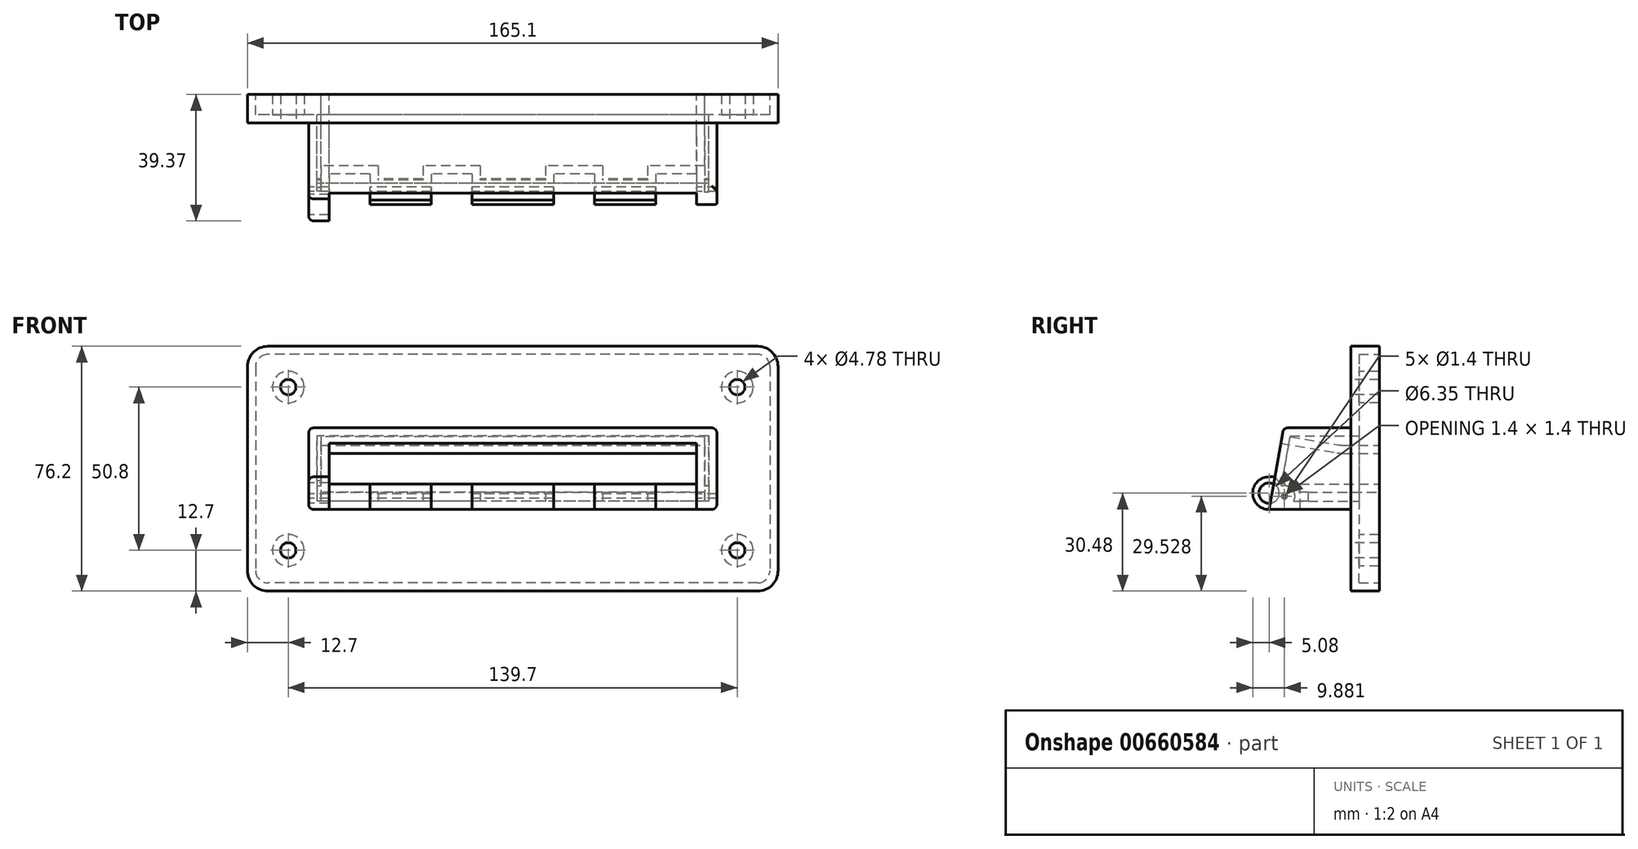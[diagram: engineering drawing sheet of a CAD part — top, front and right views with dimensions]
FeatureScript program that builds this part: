
annotation { "Feature Type Name" : "Feature", "Feature Type Description" : "" }
export const myFeature = defineFeature(function(context is Context, id is Id, definition is map)
    precondition{}
    {
        {
            var Q0;
            Q0=qCreatedBy(makeId("Front.planeOp"),FACE);
            var sketch = newSketch(context, id + "F0", { "sketchPlane" : qUnion([Q0])});
            skLineSegment(sketch, "E0.bottom", {"start": v(82.55, 38.1) * mm, "end": v(-82.55, 38.1) * mm});
            skLineSegment(sketch, "E0.top", {"start": v(82.55, -38.1) * mm, "end": v(-82.55, -38.1) * mm});
            skLineSegment(sketch, "E0.left", {"start": v(82.55, 38.1) * mm, "end": v(82.55, -38.1) * mm});
            skLineSegment(sketch, "E0.right", {"start": v(-82.55, 38.1) * mm, "end": v(-82.55, -38.1) * mm});
            skPoint(sketch, "E0.middle", {"position": v(0, 0) * mm});
            skSolve(sketch);
        }
        {
            var Q0;
            Q0=makeQuery(id+"F0.imprint","IMPRINT",FACE,{"disambiguationData":[TD([[makeQuery(id+"F0.imprint","IMPRINT",EDGE,{"derivedFrom":sQuery(id+"F0.wireOp",EDGE,"E0.bottom")}),1.0]])]});
            extrude(context, id + "F1", {"entities" : qUnion([Q0]), "depth" : 34.3 * mm, "offsetDistance" : 25.4 * mm});
        }
        {
            var Q0;
            Q0=makeQuery(id+"F1.opExtrude","CAP_FACE",FACE,{"disambiguationData":[OSD([sQuery(id+"F0.wireOp",EDGE,"E0.bottom"),sQuery(id+"F0.wireOp",EDGE,"E0.top"),sQuery(id+"F0.wireOp",EDGE,"E0.left"),sQuery(id+"F0.wireOp",EDGE,"E0.right")])],"isStart":false});
            var sketch = newSketch(context, id + "F2", { "sketchPlane" : qUnion([Q0])});
            skLineSegment(sketch, "E1.bottom", {"start": v(63.5, 12.7) * mm, "end": v(-63.5, 12.7) * mm});
            skLineSegment(sketch, "E1.top", {"start": v(63.5, -12.7) * mm, "end": v(-63.5, -12.7) * mm});
            skLineSegment(sketch, "E1.left", {"start": v(63.5, 12.7) * mm, "end": v(63.5, -12.7) * mm});
            skLineSegment(sketch, "E1.right", {"start": v(-63.5, 12.7) * mm, "end": v(-63.5, -12.7) * mm});
            skPoint(sketch, "E1.middle", {"position": v(0, 0) * mm});
            skLineSegment(sketch, "E2.bottom", {"start": v(82.55, 38.1) * mm, "end": v(-82.55, 38.1) * mm});
            skLineSegment(sketch, "E2.top", {"start": v(82.55, -38.1) * mm, "end": v(-82.55, -38.1) * mm});
            skLineSegment(sketch, "E2.left", {"start": v(82.55, 38.1) * mm, "end": v(82.55, -38.1) * mm});
            skLineSegment(sketch, "E2.right", {"start": v(-82.55, 38.1) * mm, "end": v(-82.55, -38.1) * mm});
            skSolve(sketch);
        }
        {
            var Q0;
            Q0=makeQuery(id+"F2.imprint","IMPRINT",FACE,{"disambiguationData":[TD([[makeQuery(id+"F2.imprint","IMPRINT",EDGE,{"derivedFrom":sQuery(id+"F2.wireOp",EDGE,"E1.bottom")}),-1.0]])]});
            extrude(context, id + "F3", {"entities" : qUnion([Q0]), "operationType" : NewBodyOperationType.REMOVE, "oppositeDirection" : true, "depth" : 25.4 * mm, "offsetDistance" : 25.4 * mm});
        }
        {
            var Q0;
            Q0=makeQuery(id+"F1.opExtrude","CAP_FACE",FACE,{"disambiguationData":[OSD([sQuery(id+"F0.wireOp",EDGE,"E0.bottom"),sQuery(id+"F0.wireOp",EDGE,"E0.top"),sQuery(id+"F0.wireOp",EDGE,"E0.left"),sQuery(id+"F0.wireOp",EDGE,"E0.right")])],"isStart":true});
            var sketch = newSketch(context, id + "F4", { "sketchPlane" : qUnion([Q0])});
            skLineSegment(sketch, "E3.bottom", {"start": v(57.15, 4.76) * mm, "end": v(-57.15, 4.76) * mm});
            skLineSegment(sketch, "E3.top", {"start": v(57.15, -4.76) * mm, "end": v(-57.15, -4.76) * mm});
            skLineSegment(sketch, "E3.left", {"start": v(57.15, 4.76) * mm, "end": v(57.15, -4.76) * mm});
            skLineSegment(sketch, "E3.right", {"start": v(-57.15, 4.76) * mm, "end": v(-57.15, -4.76) * mm});
            skPoint(sketch, "E3.middle", {"position": v(0, 0) * mm});
            skSolve(sketch);
        }
        {
            var Q0;
            Q0=makeQuery(id+"F4.imprint","IMPRINT",FACE,{"disambiguationData":[TD([[makeQuery(id+"F4.imprint","IMPRINT",EDGE,{"derivedFrom":sQuery(id+"F4.wireOp",EDGE,"E3.bottom")}),1.0]])]});
            extrude(context, id + "F5", {"entities" : qUnion([Q0]), "operationType" : NewBodyOperationType.REMOVE, "endBound" : BoundingType.THROUGH_ALL, "oppositeDirection" : true, "depth" : 25.4 * mm, "offsetDistance" : 25.4 * mm});
        }
        {
            var Q0;
            Q0=makeQuery(id+"F1.opExtrude","CAP_FACE",FACE,{"disambiguationData":[OSD([sQuery(id+"F0.wireOp",EDGE,"E0.bottom"),sQuery(id+"F0.wireOp",EDGE,"E0.top"),sQuery(id+"F0.wireOp",EDGE,"E0.left"),sQuery(id+"F0.wireOp",EDGE,"E0.right")])],"isStart":false});
            var sketch = newSketch(context, id + "F6", { "sketchPlane" : qUnion([Q0])});
            skLineSegment(sketch, "E4.bottom", {"start": v(-57.15, -4.76) * mm, "end": v(-44.45, -4.76) * mm});
            skLineSegment(sketch, "E4.top", {"start": v(-57.15, -12.7) * mm, "end": v(-44.45, -12.7) * mm});
            skLineSegment(sketch, "E4.left", {"start": v(-57.15, -4.76) * mm, "end": v(-57.15, -12.7) * mm});
            skLineSegment(sketch, "E4.right", {"start": v(-44.45, -4.76) * mm, "end": v(-44.45, -12.7) * mm});
            skLineSegment(sketch, "E5.bottom", {"start": v(57.15, -4.76) * mm, "end": v(44.45, -4.76) * mm});
            skLineSegment(sketch, "E5.top", {"start": v(57.15, -12.7) * mm, "end": v(44.45, -12.7) * mm});
            skLineSegment(sketch, "E5.left", {"start": v(57.15, -4.76) * mm, "end": v(57.15, -12.7) * mm});
            skLineSegment(sketch, "E5.right", {"start": v(44.45, -4.76) * mm, "end": v(44.45, -12.7) * mm});
            skLineSegment(sketch, "E6.bottom", {"start": v(-25.4, -4.76) * mm, "end": v(-12.7, -4.76) * mm});
            skLineSegment(sketch, "E6.top", {"start": v(-25.4, -12.7) * mm, "end": v(-12.7, -12.7) * mm});
            skLineSegment(sketch, "E6.left", {"start": v(-25.4, -4.76) * mm, "end": v(-25.4, -12.7) * mm});
            skLineSegment(sketch, "E6.right", {"start": v(-12.7, -4.76) * mm, "end": v(-12.7, -12.7) * mm});
            skLineSegment(sketch, "E7.bottom", {"start": v(12.7, -4.76) * mm, "end": v(25.4, -4.76) * mm});
            skLineSegment(sketch, "E7.top", {"start": v(12.7, -12.7) * mm, "end": v(25.4, -12.7) * mm});
            skLineSegment(sketch, "E7.left", {"start": v(12.7, -4.76) * mm, "end": v(12.7, -12.7) * mm});
            skLineSegment(sketch, "E7.right", {"start": v(25.4, -4.76) * mm, "end": v(25.4, -12.7) * mm});
            skSolve(sketch);
        }
        {
            var Q0;
            Q0=makeQuery(id+"F6.imprint","IMPRINT",FACE,{"disambiguationData":[TD([[makeQuery(id+"F6.imprint","IMPRINT",EDGE,{"derivedFrom":sQuery(id+"F6.wireOp",EDGE,"E4.bottom")}),1.0]])]});
            var Q1;
            Q1=makeQuery(id+"F6.imprint","IMPRINT",FACE,{"disambiguationData":[TD([[makeQuery(id+"F6.imprint","IMPRINT",EDGE,{"derivedFrom":sQuery(id+"F6.wireOp",EDGE,"E6.bottom")}),1.0]])]});
            var Q2;
            Q2=makeQuery(id+"F6.imprint","IMPRINT",FACE,{"disambiguationData":[TD([[makeQuery(id+"F6.imprint","IMPRINT",EDGE,{"derivedFrom":sQuery(id+"F6.wireOp",EDGE,"E7.bottom")}),1.0]])]});
            var Q3;
            Q3=makeQuery(id+"F6.imprint","IMPRINT",FACE,{"disambiguationData":[TD([[makeQuery(id+"F6.imprint","IMPRINT",EDGE,{"derivedFrom":sQuery(id+"F6.wireOp",EDGE,"E5.bottom")}),1.0]])]});
            extrude(context, id + "F7", {"entities" : qUnion([Q0, Q1, Q2, Q3]), "operationType" : NewBodyOperationType.REMOVE, "oppositeDirection" : true, "depth" : 9.52 * mm, "offsetDistance" : 25.4 * mm});
        }
        {
            var Q0;
            Q0=makeQuery(id+"F3.boolean.opBoolean","COPY",FACE,{"derivedFrom":makeQuery(id+"F3.opExtrude","SWEPT_FACE",FACE,{"disambiguationData":[OSD([sQuery(id+"F2.wireOp",EDGE,"E1.left")])]})});
            var sketch = newSketch(context, id + "F8", { "sketchPlane" : qUnion([Q0])});
            skLineSegment(sketch, "E8", {"start": v(-34.3, -12.7) * mm, "end": v(-29.81, 12.7) * mm});
            skLineSegment(sketch, "E9", {"start": v(-29.81, 12.7) * mm, "end": v(-34.3, 12.7) * mm});
            skLineSegment(sketch, "E10", {"start": v(-34.3, 12.7) * mm, "end": v(-34.3, -12.7) * mm});
            skSolve(sketch);
        }
        {
            var Q0;
            Q0=makeQuery(id+"F8.imprint","IMPRINT",FACE,{"disambiguationData":[TD([[makeQuery(id+"F8.imprint","IMPRINT",EDGE,{"derivedFrom":sQuery(id+"F8.wireOp",EDGE,"E8")}),1.0]])]});
            extrude(context, id + "F9", {"entities" : qUnion([Q0]), "operationType" : NewBodyOperationType.REMOVE, "endBound" : BoundingType.THROUGH_ALL, "oppositeDirection" : true, "depth" : 25.4 * mm, "offsetDistance" : 25.4 * mm});
        }
        {
            var Q0;
            Q0=makeQuery(id+"F3.boolean.opBoolean","COPY",FACE,{"derivedFrom":makeQuery(id+"F3.opExtrude","SWEPT_FACE",FACE,{"disambiguationData":[OSD([sQuery(id+"F2.wireOp",EDGE,"E1.right")])]})});
            var sketch = newSketch(context, id + "F10", { "sketchPlane" : qUnion([Q0])});
            skArc(sketch, "E11", {"start": v(34.3, -12.7) * mm, "mid": v(39.37, -7.62) * mm, "end": v(34.3, -2.54) * mm});
            skLineSegment(sketch, "E12", {"start": v(34.3, -2.54) * mm, "end": v(32.5, -2.54) * mm});
            skLineSegment(sketch, "E13", {"start": v(32.5, -2.54) * mm, "end": v(34.3, -12.7) * mm});
            skSolve(sketch);
        }
        {
            var Q0;
            Q0=makeQuery(id+"F10.imprint","IMPRINT",FACE,{"disambiguationData":[TD([[makeQuery(id+"F10.imprint","IMPRINT",EDGE,{"derivedFrom":sQuery(id+"F10.wireOp",EDGE,"E11")}),1.0]])]});
            extrude(context, id + "F11", {"entities" : qUnion([Q0]), "operationType" : NewBodyOperationType.ADD, "oppositeDirection" : true, "depth" : 6.35 * mm, "offsetDistance" : 25.4 * mm});
        }
        {
            var Q0;
            Q0=makeQuery(id+"F11.boolean.opBoolean","MERGE",FACE,{"derivedFrom":[makeQuery(id+"F3.boolean.opBoolean","COPY",FACE,{"derivedFrom":makeQuery(id+"F3.opExtrude","SWEPT_FACE",FACE,{"disambiguationData":[OSD([sQuery(id+"F2.wireOp",EDGE,"E1.right")])]})}),makeQuery(id+"F11.opExtrude","CAP_FACE",FACE,{"disambiguationData":[OSD([sQuery(id+"F10.wireOp",EDGE,"E11"),sQuery(id+"F10.wireOp",EDGE,"t9ToSJXX-xxId-XsRl-dtjL-8FJcNpwY83Oj"),sQuery(id+"F10.wireOp",EDGE,"S0cJsciV-L8RJ-brYd-5tid-K804BzsuG4tW")])],"isStart":true})]});
            var sketch = newSketch(context, id + "F12", { "sketchPlane" : qUnion([Q0])});
            skPoint(sketch, "E14", {"position": v(34.3, -7.62) * mm});
            skPoint(sketch, "E15", {"position": v(40.8, -7.72) * mm});
            skSolve(sketch);
        }
        {
            var Q0;
            Q0=sQuery(id+"F12.wireOp",VERTEX,"E14");
            var Q1;
            Q1=makeQuery(id+"F1.opExtrude","SWEPT_BODY",BODY,{"disambiguationData":[OSD([sQuery(id+"F0.wireOp",EDGE,"E0.bottom"),sQuery(id+"F0.wireOp",EDGE,"E0.top"),sQuery(id+"F0.wireOp",EDGE,"E0.left"),sQuery(id+"F0.wireOp",EDGE,"E0.right")])]});
            hole(context, id + "F13", {"style" : HoleStyle.SIMPLE, "endStyle" : HoleEndStyle.BLIND, "holeDiameter" : 6.35 * mm, "majorDiameter" : 6.35 * mm, "holeDepth" : 13.97 * mm, "isTappedThrough" : true, "tappedDepth" : 12.7 * mm, "tapClearance" : 3, "startFromSketch" : true, "locations" : qUnion([Q0]), "scope" : qUnion([Q1])});
        }
        {
            var Q0;
            Q0=makeQuery(id+"F1.opExtrude","SWEPT_EDGE",EDGE,{"disambiguationData":[OSD([sQuery(id+"F0.wireOp",EDGE,"E0.bottom"),sQuery(id+"F0.wireOp",EDGE,"E0.right")])]});
            var Q1;
            Q1=makeQuery(id+"F1.opExtrude","SWEPT_EDGE",EDGE,{"disambiguationData":[OSD([sQuery(id+"F0.wireOp",EDGE,"E0.bottom"),sQuery(id+"F0.wireOp",EDGE,"E0.left")])]});
            var Q2;
            Q2=makeQuery(id+"F1.opExtrude","SWEPT_EDGE",EDGE,{"disambiguationData":[OSD([sQuery(id+"F0.wireOp",EDGE,"E0.top"),sQuery(id+"F0.wireOp",EDGE,"E0.left")])]});
            var Q3;
            Q3=makeQuery(id+"F1.opExtrude","SWEPT_EDGE",EDGE,{"disambiguationData":[OSD([sQuery(id+"F0.wireOp",EDGE,"E0.top"),sQuery(id+"F0.wireOp",EDGE,"E0.right")])]});
            fillet(context, id + "F14", {"entities" : qUnion([Q0, Q1, Q2, Q3]), "radius" : 6.35 * mm, "tangentPropagation" : true, "allowEdgeOverflow" : false});
        }
        {
            var Q0;
            Q0=makeQuery(id+"F9.boolean.opBoolean","INTERSECT",EDGE,{"derivedFrom":[makeQuery(id+"F5.boolean.opBoolean","COPY",FACE,{"derivedFrom":makeQuery(id+"F5.opExtrude","SWEPT_FACE",FACE,{"disambiguationData":[OSD([sQuery(id+"F4.wireOp",EDGE,"E3.bottom")])]})}),makeQuery(id+"F9.opExtrude","SWEPT_FACE",FACE,{"disambiguationData":[OSD([sQuery(id+"F8.wireOp",EDGE,"E8")])]})]});
            chamfer(context, id + "F15", {"entities" : qUnion([Q0]), "chamferType" : ChamferType.TWO_OFFSETS, "width1" : 19.05 * mm, "oppositeDirection" : false, "width2" : 3.17 * mm, "tangentPropagation" : true});
        }
        {
            var Q0;
            Q0=makeQuery(id+"F3.boolean.opBoolean","COPY",FACE,{"derivedFrom":makeQuery(id+"F3.opExtrude","CAP_FACE",FACE,{"disambiguationData":[OSD([sQuery(id+"F2.wireOp",EDGE,"E1.bottom"),sQuery(id+"F2.wireOp",EDGE,"E1.top"),sQuery(id+"F2.wireOp",EDGE,"E1.left"),sQuery(id+"F2.wireOp",EDGE,"E1.right"),sQuery(id+"F2.wireOp",EDGE,"E2.bottom"),sQuery(id+"F2.wireOp",EDGE,"E2.top"),sQuery(id+"F2.wireOp",EDGE,"E2.left"),sQuery(id+"F2.wireOp",EDGE,"E2.right")])],"isStart":false})});
            var sketch = newSketch(context, id + "F16", { "sketchPlane" : qUnion([Q0])});
            skPoint(sketch, "E16", {"position": v(-69.85, 25.4) * mm});
            skPoint(sketch, "E17", {"position": v(69.85, 25.4) * mm});
            skPoint(sketch, "E18", {"position": v(69.85, -25.4) * mm});
            skPoint(sketch, "E19", {"position": v(-69.85, -25.4) * mm});
            skSolve(sketch);
        }
        {
            var Q0;
            Q0=sQuery(id+"F16.wireOp",VERTEX,"E16");
            var Q1;
            Q1=sQuery(id+"F16.wireOp",VERTEX,"E17");
            var Q2;
            Q2=sQuery(id+"F16.wireOp",VERTEX,"E18");
            var Q3;
            Q3=sQuery(id+"F16.wireOp",VERTEX,"E19");
            var Q4;
            Q4=makeQuery(id+"F1.opExtrude","SWEPT_BODY",BODY,{"disambiguationData":[OSD([sQuery(id+"F0.wireOp",EDGE,"E0.bottom"),sQuery(id+"F0.wireOp",EDGE,"E0.top"),sQuery(id+"F0.wireOp",EDGE,"E0.left"),sQuery(id+"F0.wireOp",EDGE,"E0.right")])]});
            hole(context, id + "F17", {"style" : HoleStyle.SIMPLE, "endStyle" : HoleEndStyle.THROUGH, "holeDiameter" : 4.78 * mm, "majorDiameter" : 6.35 * mm, "isTappedThrough" : true, "tappedDepth" : 12.7 * mm, "tapClearance" : 3, "startFromSketch" : true, "locations" : qUnion([Q0, Q1, Q2, Q3]), "scope" : qUnion([Q4])});
        }
        {
            var Q0;
            Q0=makeQuery(id+"F11.boolean.opBoolean","MERGE",FACE,{"derivedFrom":[makeQuery(id+"F3.boolean.opBoolean","COPY",FACE,{"derivedFrom":makeQuery(id+"F3.opExtrude","SWEPT_FACE",FACE,{"disambiguationData":[OSD([sQuery(id+"F2.wireOp",EDGE,"E1.right")])]})}),makeQuery(id+"F11.opExtrude","CAP_FACE",FACE,{"disambiguationData":[OSD([sQuery(id+"F10.wireOp",EDGE,"E11"),sQuery(id+"F10.wireOp",EDGE,"t9ToSJXX-xxId-XsRl-dtjL-8FJcNpwY83Oj"),sQuery(id+"F10.wireOp",EDGE,"S0cJsciV-L8RJ-brYd-5tid-K804BzsuG4tW")])],"isStart":true})]});
            var sketch = newSketch(context, id + "F18", { "sketchPlane" : qUnion([Q0])});
            skPoint(sketch, "E20", {"position": v(29.49, -8.57) * mm});
            skSolve(sketch);
        }
        {
            var Q0;
            Q0=sQuery(id+"F18.wireOp",VERTEX,"E20");
            var Q1;
            Q1=makeQuery(id+"F1.opExtrude","SWEPT_BODY",BODY,{"disambiguationData":[OSD([sQuery(id+"F0.wireOp",EDGE,"E0.bottom"),sQuery(id+"F0.wireOp",EDGE,"E0.top"),sQuery(id+"F0.wireOp",EDGE,"E0.left"),sQuery(id+"F0.wireOp",EDGE,"E0.right")])]});
            hole(context, id + "F19", {"style" : HoleStyle.SIMPLE, "endStyle" : HoleEndStyle.THROUGH, "holeDiameter" : 1.4 * mm, "majorDiameter" : 6.35 * mm, "isTappedThrough" : true, "tappedDepth" : 12.7 * mm, "tapClearance" : 3, "startFromSketch" : true, "locations" : qUnion([Q0]), "scope" : qUnion([Q1])});
        }
        {
            var Q0;
            Q0=makeQuery(id+"F9.boolean.opBoolean","INTERSECT",EDGE,{"derivedFrom":[makeQuery(id+"F3.boolean.opBoolean","COPY",FACE,{"derivedFrom":makeQuery(id+"F3.opExtrude","SWEPT_FACE",FACE,{"disambiguationData":[OSD([sQuery(id+"F2.wireOp",EDGE,"E1.right")])]})}),makeQuery(id+"F9.opExtrude","SWEPT_FACE",FACE,{"disambiguationData":[OSD([sQuery(id+"F8.wireOp",EDGE,"E8")])]})]});
            fillet(context, id + "F20", {"entities" : qUnion([Q0]), "radius" : 1.59 * mm, "tangentPropagation" : true, "allowEdgeOverflow" : false});
        }
        {
            var Q0;
            Q0=makeQuery(id+"F3.boolean.opBoolean","COPY",EDGE,{"derivedFrom":makeQuery(id+"F3.opExtrude","SWEPT_EDGE",EDGE,{"disambiguationData":[OSD([sQuery(id+"F2.wireOp",EDGE,"E1.bottom"),sQuery(id+"F2.wireOp",EDGE,"E1.right")])]})});
            var Q1;
            Q1=makeQuery(id+"F3.boolean.opBoolean","COPY",EDGE,{"derivedFrom":makeQuery(id+"F3.opExtrude","SWEPT_EDGE",EDGE,{"disambiguationData":[OSD([sQuery(id+"F2.wireOp",EDGE,"E1.bottom"),sQuery(id+"F2.wireOp",EDGE,"E1.left")])]})});
            var Q2;
            Q2=makeQuery(id+"F3.boolean.opBoolean","COPY",EDGE,{"derivedFrom":makeQuery(id+"F3.opExtrude","SWEPT_EDGE",EDGE,{"disambiguationData":[OSD([sQuery(id+"F2.wireOp",EDGE,"E1.top"),sQuery(id+"F2.wireOp",EDGE,"E1.left")])]})});
            var Q3;
            Q3=makeQuery(id+"F3.boolean.opBoolean","COPY",EDGE,{"derivedFrom":makeQuery(id+"F3.opExtrude","SWEPT_EDGE",EDGE,{"disambiguationData":[OSD([sQuery(id+"F2.wireOp",EDGE,"E1.top"),sQuery(id+"F2.wireOp",EDGE,"E1.right")])]})});
            fillet(context, id + "F21", {"entities" : qUnion([Q0, Q1, Q2, Q3]), "radius" : 1.59 * mm, "tangentPropagation" : true, "allowEdgeOverflow" : false});
        }
        {
            var Q0;
            {var subQ0=sQuery(id+"F8.wireOp",EDGE,"E8");Q0=makeQuery(id+"F2j6ox91vYMW6DV_1.opChamfer","BLEND_EDGE",EDGE,{"blendedFrom":[makeQuery(id+"F9.boolean.opBoolean","INTERSECT",EDGE,{"derivedFrom":[makeQuery(id+"F5.boolean.opBoolean","COPY",FACE,{"derivedFrom":makeQuery(id+"F5.opExtrude","SWEPT_FACE",FACE,{"disambiguationData":[OSD([sQuery(id+"F4.wireOp",EDGE,"E3.left")])]})}),makeQuery(id+"F9.opExtrude","SWEPT_FACE",FACE,{"disambiguationData":[OSD([subQ0])]})]}),makeQuery(id+"F15.opChamfer","BLEND_FACE",FACE,{"disambiguationData":[OSD([sQuery(id+"F4.wireOp",EDGE,"E3.bottom"),subQ0])]})],"blendedInto":[makeQuery(id+"F15.opChamfer","BLEND_FACE",FACE,{"disambiguationData":[OSD([sQuery(id+"F4.wireOp",EDGE,"E3.bottom"),subQ0])]})]});}
            var Q1;
            {var subQ0=sQuery(id+"F8.wireOp",EDGE,"E8");Q1=makeQuery(id+"F2j6ox91vYMW6DV_1.opChamfer","BLEND_EDGE",EDGE,{"blendedFrom":[makeQuery(id+"F9.boolean.opBoolean","INTERSECT",EDGE,{"derivedFrom":[makeQuery(id+"F5.boolean.opBoolean","COPY",FACE,{"derivedFrom":makeQuery(id+"F5.opExtrude","SWEPT_FACE",FACE,{"disambiguationData":[OSD([sQuery(id+"F4.wireOp",EDGE,"E3.left")])]})}),makeQuery(id+"F9.opExtrude","SWEPT_FACE",FACE,{"disambiguationData":[OSD([subQ0])]})]}),makeQuery(id+"FDbppE0EpAkwhRO_1.opChamfer","BLEND_FACE",FACE,{"disambiguationData":[OSD([sQuery(id+"F4.wireOp",EDGE,"E3.top"),subQ0])]})],"blendedInto":[makeQuery(id+"FDbppE0EpAkwhRO_1.opChamfer","BLEND_FACE",FACE,{"disambiguationData":[OSD([sQuery(id+"F4.wireOp",EDGE,"E3.top"),subQ0])]})]});}
            var Q2;
            {var subQ0=sQuery(id+"F8.wireOp",EDGE,"E8");Q2=makeQuery(id+"F2j6ox91vYMW6DV_1.opChamfer","BLEND_EDGE",EDGE,{"blendedFrom":[makeQuery(id+"F9.boolean.opBoolean","INTERSECT",EDGE,{"derivedFrom":[makeQuery(id+"F5.boolean.opBoolean","COPY",FACE,{"derivedFrom":makeQuery(id+"F5.opExtrude","SWEPT_FACE",FACE,{"disambiguationData":[OSD([sQuery(id+"F4.wireOp",EDGE,"E3.right")])]})}),makeQuery(id+"F9.opExtrude","SWEPT_FACE",FACE,{"disambiguationData":[OSD([subQ0])]})]}),makeQuery(id+"FDbppE0EpAkwhRO_1.opChamfer","BLEND_FACE",FACE,{"disambiguationData":[OSD([sQuery(id+"F4.wireOp",EDGE,"E3.top"),subQ0])]})],"blendedInto":[makeQuery(id+"FDbppE0EpAkwhRO_1.opChamfer","BLEND_FACE",FACE,{"disambiguationData":[OSD([sQuery(id+"F4.wireOp",EDGE,"E3.top"),subQ0])]})]});}
            var Q3;
            {var subQ0=sQuery(id+"F8.wireOp",EDGE,"E8");Q3=makeQuery(id+"F2j6ox91vYMW6DV_1.opChamfer","BLEND_EDGE",EDGE,{"blendedFrom":[makeQuery(id+"F9.boolean.opBoolean","INTERSECT",EDGE,{"derivedFrom":[makeQuery(id+"F5.boolean.opBoolean","COPY",FACE,{"derivedFrom":makeQuery(id+"F5.opExtrude","SWEPT_FACE",FACE,{"disambiguationData":[OSD([sQuery(id+"F4.wireOp",EDGE,"E3.right")])]})}),makeQuery(id+"F9.opExtrude","SWEPT_FACE",FACE,{"disambiguationData":[OSD([subQ0])]})]}),makeQuery(id+"F15.opChamfer","BLEND_FACE",FACE,{"disambiguationData":[OSD([sQuery(id+"F4.wireOp",EDGE,"E3.bottom"),subQ0])]})],"blendedInto":[makeQuery(id+"F15.opChamfer","BLEND_FACE",FACE,{"disambiguationData":[OSD([sQuery(id+"F4.wireOp",EDGE,"E3.bottom"),subQ0])]})]});}
            var Q4;
            {var subQ0=makeQuery(id+"F5.boolean.opBoolean","COPY",FACE,{"derivedFrom":makeQuery(id+"F5.opExtrude","SWEPT_FACE",FACE,{"disambiguationData":[OSD([sQuery(id+"F4.wireOp",EDGE,"E3.left")])]})});Q4=makeQuery(id+"F2j6ox91vYMW6DV_1.opChamfer","BLEND_EDGE",EDGE,{"blendedFrom":[makeQuery(id+"F9.boolean.opBoolean","INTERSECT",EDGE,{"derivedFrom":[subQ0,makeQuery(id+"F9.opExtrude","SWEPT_FACE",FACE,{"disambiguationData":[OSD([sQuery(id+"F8.wireOp",EDGE,"E8")])]})]}),subQ0],"blendedInto":[subQ0]});}
            var Q5;
            {var subQ0=makeQuery(id+"F5.boolean.opBoolean","COPY",FACE,{"derivedFrom":makeQuery(id+"F5.opExtrude","SWEPT_FACE",FACE,{"disambiguationData":[OSD([sQuery(id+"F4.wireOp",EDGE,"E3.right")])]})});Q5=makeQuery(id+"F2j6ox91vYMW6DV_1.opChamfer","BLEND_EDGE",EDGE,{"blendedFrom":[makeQuery(id+"F9.boolean.opBoolean","INTERSECT",EDGE,{"derivedFrom":[subQ0,makeQuery(id+"F9.opExtrude","SWEPT_FACE",FACE,{"disambiguationData":[OSD([sQuery(id+"F8.wireOp",EDGE,"E8")])]})]}),subQ0],"blendedInto":[subQ0]});}
            var Q6;
            {var subQ0=makeQuery(id+"F5.boolean.opBoolean","COPY",FACE,{"derivedFrom":makeQuery(id+"F5.opExtrude","SWEPT_FACE",FACE,{"disambiguationData":[OSD([sQuery(id+"F4.wireOp",EDGE,"E3.top")])]})});Q6=makeQuery(id+"FDbppE0EpAkwhRO_1.opChamfer","BLEND_EDGE",EDGE,{"blendedFrom":[makeQuery(id+"F9.boolean.opBoolean","INTERSECT",EDGE,{"derivedFrom":[subQ0,makeQuery(id+"F9.opExtrude","SWEPT_FACE",FACE,{"disambiguationData":[OSD([sQuery(id+"F8.wireOp",EDGE,"E8")])]})]}),subQ0],"blendedInto":[subQ0]});}
            var Q7;
            {var subQ0=makeQuery(id+"F5.boolean.opBoolean","COPY",FACE,{"derivedFrom":makeQuery(id+"F5.opExtrude","SWEPT_FACE",FACE,{"disambiguationData":[OSD([sQuery(id+"F4.wireOp",EDGE,"E3.bottom")])]})});Q7=makeQuery(id+"F15.opChamfer","BLEND_EDGE",EDGE,{"blendedFrom":[makeQuery(id+"F9.boolean.opBoolean","INTERSECT",EDGE,{"derivedFrom":[subQ0,makeQuery(id+"F9.opExtrude","SWEPT_FACE",FACE,{"disambiguationData":[OSD([sQuery(id+"F8.wireOp",EDGE,"E8")])]})]}),subQ0],"blendedInto":[subQ0]});}
            fillet(context, id + "F22", {"entities" : qUnion([Q0, Q1, Q2, Q3, Q4, Q5, Q6, Q7]), "radius" : 12.7 * mm, "tangentPropagation" : true, "allowEdgeOverflow" : false});
        }
        {
            var Q0;
            Q0=makeQuery(id+"F1.opExtrude","CAP_FACE",FACE,{"disambiguationData":[OSD([sQuery(id+"F0.wireOp",EDGE,"E0.bottom"),sQuery(id+"F0.wireOp",EDGE,"E0.top"),sQuery(id+"F0.wireOp",EDGE,"E0.left"),sQuery(id+"F0.wireOp",EDGE,"E0.right")])],"isStart":true});
            shell(context, id + "F23", {"entities" : qUnion([Q0]), "thickness" : 2.54 * mm});
        }
    });
